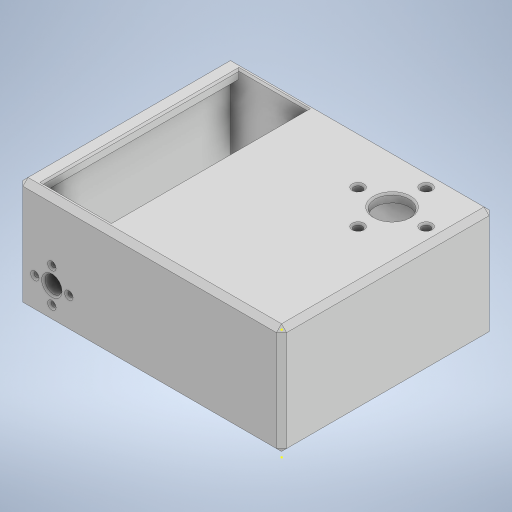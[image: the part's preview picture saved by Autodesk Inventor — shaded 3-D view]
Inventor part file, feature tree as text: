
AUTODESK INVENTOR PART (.ipt)
format: ipt  version: 2023 (Build 270158000, 158)  size: 327,680 bytes
history: native  units: mm
features: sketch x16, extrude x10, chamfer x4
ambient origin geometry x8: Origin, YZ Plane, XZ Plane, XY Plane, X Axis, Y Axis, Z Axis, Center Point
bodies: Solid1 (feature_tree)
feature tree (30):
  extrude  "Extrusion1"  Depth=155.0mm
  extrude  "Extrusion2"  Depth=5.0mm
  extrude  "Extrusion3"  Depth=5.0mm
  extrude  "Extrusion4"  Depth=55.0mm TaperAngle=0.0deg
  extrude  "Extrusion5"  Depth=5.0mm
  extrude  "Extrusion6"  Depth=30.0mm
  extrude  "Extrusion7"  Depth=5.0mm
  sketch  "Sketch8"  dims[d18=20.0mm d19=10.0mm d20=20.0mm d21=0.0mm]
  sketch  "Sketch9"  dims[d22=10.0mm]
  sketch  "Sketch10"  dims[d23=5.0mm]
  extrude  "Extrusion8"  Depth=10.0mm
  chamfer  "Chamfer1"  Distance=20.0mm
  chamfer  "Chamfer3"  Distance=5.0mm
  extrude  "Extrusion9"  Depth=40.0mm TaperAngle=360.0deg
  sketch  "Sketch13"  dims[d28=3.0mm d29=40.0mm d31=360.0deg]
  extrude  "Extrusion10"  Depth=10.0mm
  chamfer  "Chamfer4"  Distance=40.0mm Angle=360.0deg
  chamfer  "Chamfer5"  Distance=5.0mm
  sketch  "Sketch15"  dims[d36=20.0mm]
  sketch  "Sketch16"  dims[d37=5.0mm d38=40.0mm d40=360.0deg d42=5.0mm d43=0.0mm d44=1.0mm d45=2.0mm d46=45.0deg d50=1.0mm d51=2.0mm d52=45.0deg d53=30.0mm d54=30.0mm d55=5.0mm d56=0.0mm d57=20.0mm d58=0.0mm d59=1.0mm d60=2.0mm d61=45.0deg d62=3.0mm d63=2.0mm d64=45.0deg d30=0.872665mm d32=0.872665mm]
  sketch  "Sketch1"  dims[d0=125.0mm d1=155.0mm]
  sketch  "Sketch2"  dims[d2=60.0mm d3=0.0mm d4=5.0mm]
  sketch  "Sketch3"  dims[d5=5.0mm d6=5.0mm]
  sketch  "Sketch4"  dims[d7=5.0mm d8=55.0mm d9=0.0mm]
  sketch  "Sketch5"  dims[d10=5.0mm d11=0.0mm d12=20.0mm]
  sketch  "Sketch6"  dims[d13=30.0mm d14=30.0mm]
  sketch  "Sketch7"  dims[d15=5.0mm d16=0.0mm d17=20.0mm]
  sketch  "Sketch11"  dims[d24=5.0mm]
  sketch  "Sketch12"  dims[d25=40.0mm d26=5.0mm d27=0.0mm]
  sketch  "Sketch14"  dims[d33=5.0mm d34=0.0mm d35=10.0mm]
